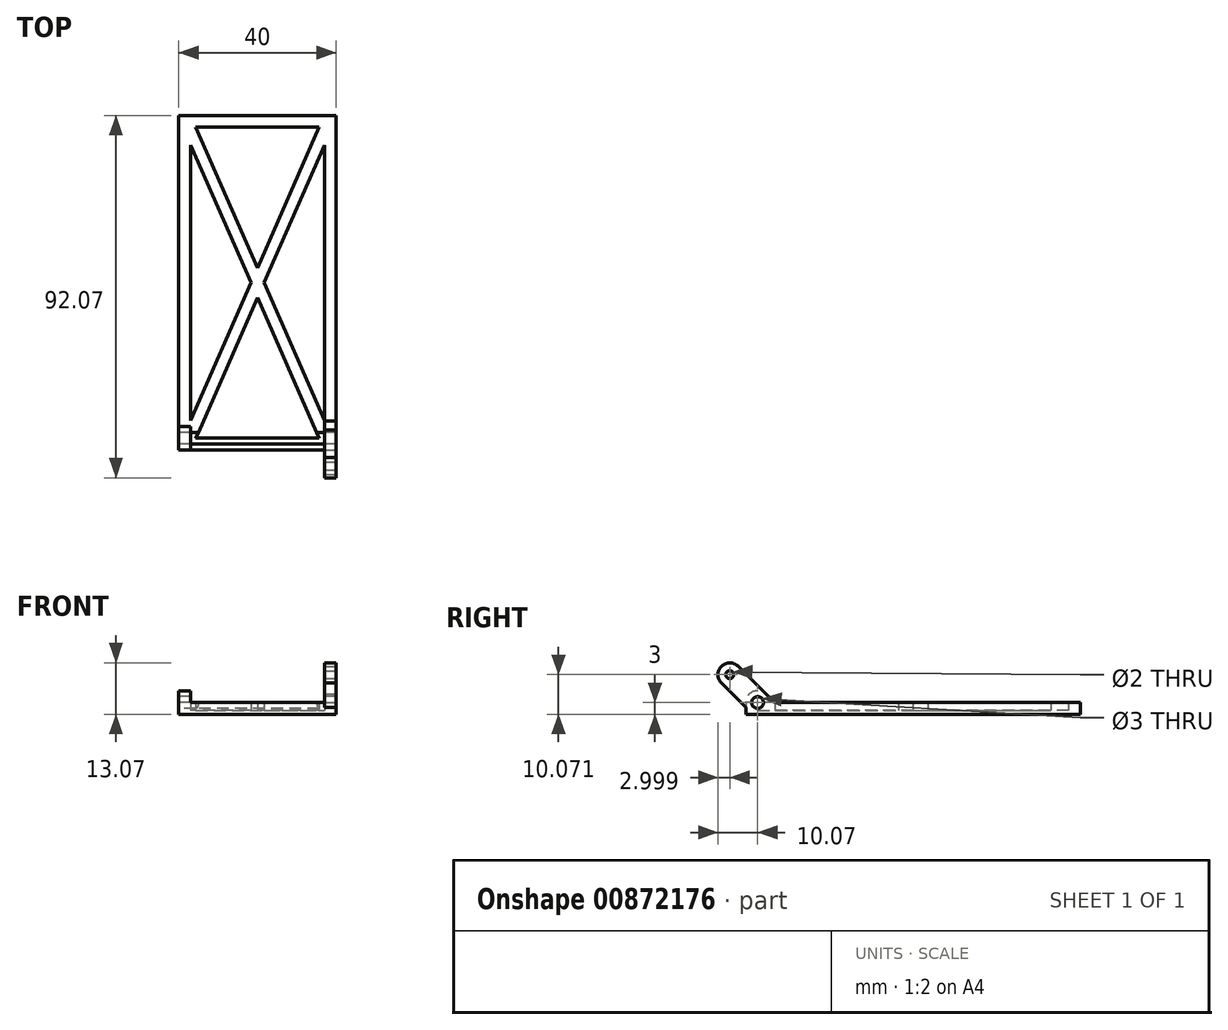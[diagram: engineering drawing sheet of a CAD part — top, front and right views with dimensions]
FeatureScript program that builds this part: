
annotation { "Feature Type Name" : "Feature", "Feature Type Description" : "" }
export const myFeature = defineFeature(function(context is Context, id is Id, definition is map)
    precondition{}
    {
        {
            var Q0;
            Q0=qCreatedBy(makeId("Top.planeOp"),FACE);
            var sketch = newSketch(context, id + "F0", { "sketchPlane" : qUnion([Q0])});
            skLineSegment(sketch, "E0.bottom", {"start": v(20, 42.5) * mm, "end": v(-20, 42.5) * mm});
            skLineSegment(sketch, "E0.top", {"start": v(20, -42.5) * mm, "end": v(-20, -42.5) * mm});
            skLineSegment(sketch, "E0.left", {"start": v(20, 42.5) * mm, "end": v(20, -42.5) * mm});
            skLineSegment(sketch, "E0.right", {"start": v(-20, 42.5) * mm, "end": v(-20, -42.5) * mm});
            skPoint(sketch, "E0.middle", {"position": v(0, 0) * mm});
            skSolve(sketch);
        }
        {
            var Q0;
            Q0=makeQuery(id+"F0.imprint","IMPRINT",FACE,{"disambiguationData":[TD([[makeQuery(id+"F0.imprint","IMPRINT",EDGE,{"derivedFrom":sQuery(id+"F0.wireOp",EDGE,"E0.bottom")}),1.0]])]});
            extrude(context, id + "F1", {"entities" : qUnion([Q0]), "depth" : 1 * mm, "offsetDistance" : 25 * mm});
        }
        {
            var Q0;
            Q0=makeQuery(id+"F1.opExtrude","CAP_FACE",FACE,{"disambiguationData":[OSD([sQuery(id+"F0.wireOp",EDGE,"E0.bottom"),sQuery(id+"F0.wireOp",EDGE,"E0.top"),sQuery(id+"F0.wireOp",EDGE,"E0.left"),sQuery(id+"F0.wireOp",EDGE,"E0.right")])],"isStart":false});
            var sketch = newSketch(context, id + "F2", { "sketchPlane" : qUnion([Q0])});
            skLineSegment(sketch, "E1.bottom", {"start": v(17, -42.5) * mm, "end": v(20, -42.5) * mm});
            skLineSegment(sketch, "E1.top", {"start": v(17, 42.5) * mm, "end": v(20, 42.5) * mm});
            skLineSegment(sketch, "E1.left", {"start": v(17, -42.5) * mm, "end": v(17, 42.5) * mm});
            skLineSegment(sketch, "E1.right", {"start": v(20, -42.5) * mm, "end": v(20, 42.5) * mm});
            skLineSegment(sketch, "E2.bottom", {"start": v(-20, -42.5) * mm, "end": v(-17, -42.5) * mm});
            skLineSegment(sketch, "E2.top", {"start": v(-20, 42.5) * mm, "end": v(-17, 42.5) * mm});
            skLineSegment(sketch, "E2.left", {"start": v(-20, -42.5) * mm, "end": v(-20, 42.5) * mm});
            skLineSegment(sketch, "E2.right", {"start": v(-17, -42.5) * mm, "end": v(-17, 42.5) * mm});
            skLineSegment(sketch, "E3", {"start": v(-17, -42.5) * mm, "end": v(17, 35.03) * mm});
            skLineSegment(sketch, "E4", {"start": v(17, 35.03) * mm, "end": v(17, 42.5) * mm});
            skLineSegment(sketch, "E5", {"start": v(17, 42.5) * mm, "end": v(-17, -35.03) * mm});
            skLineSegment(sketch, "E6", {"start": v(-17, -35.03) * mm, "end": v(-17, -42.5) * mm});
            skLineSegment(sketch, "E7", {"start": v(17, -42.5) * mm, "end": v(-17, 35.03) * mm});
            skLineSegment(sketch, "E8", {"start": v(-17, 35.03) * mm, "end": v(-17, 42.5) * mm});
            skLineSegment(sketch, "E9", {"start": v(-17, 42.5) * mm, "end": v(17, -35.03) * mm});
            skLineSegment(sketch, "E10", {"start": v(17, -35.03) * mm, "end": v(17, -42.5) * mm});
            skLineSegment(sketch, "E11.bottom", {"start": v(-20, -42.5) * mm, "end": v(20, -42.5) * mm});
            skLineSegment(sketch, "E11.top", {"start": v(-20, -39.5) * mm, "end": v(20, -39.5) * mm});
            skLineSegment(sketch, "E11.left", {"start": v(-20, -42.5) * mm, "end": v(-20, -39.5) * mm});
            skLineSegment(sketch, "E11.right", {"start": v(20, -42.5) * mm, "end": v(20, -39.5) * mm});
            skLineSegment(sketch, "E12.bottom", {"start": v(-20, 42.5) * mm, "end": v(20, 42.5) * mm});
            skLineSegment(sketch, "E12.top", {"start": v(-20, 39.5) * mm, "end": v(20, 39.5) * mm});
            skLineSegment(sketch, "E12.left", {"start": v(-20, 42.5) * mm, "end": v(-20, 39.5) * mm});
            skLineSegment(sketch, "E12.right", {"start": v(20, 42.5) * mm, "end": v(20, 39.5) * mm});
            skSolve(sketch);
        }
        {
            var Q0;
            {var subQ0=sQuery(id+"F2.wireOp",EDGE,"E11.bottom");Q0=makeQuery(id+"F2.imprint","IMPRINT",FACE,{"disambiguationData":[TD([[makeQuery(id+"F2.imprint","IMPRINT",EDGE,{"derivedFrom":subQ0}),-1.0]])]});}
            var Q1;
            {var subQ0=sQuery(id+"F2.wireOp",EDGE,"E3");var subQ3=sQuery(id+"F2.wireOp",EDGE,"E11.top");var subQ5=makeQuery(id+"F2.imprint","INTERSECT",VERTEX,{"derivedFrom":[subQ0,subQ3]});Q1=makeQuery(id+"F2.imprint","IMPRINT",FACE,{"disambiguationData":[TD([[makeQuery(id+"F2.imprint","IMPRINT",EDGE,{"disambiguationData":[TD([[subQ5,1.0]])],"derivedFrom":subQ3}),-1.0]])]});}
            var Q2;
            {var subQ0=sQuery(id+"F2.wireOp",EDGE,"E2.bottom");Q2=makeQuery(id+"F2.imprint","IMPRINT",FACE,{"disambiguationData":[TD([[makeQuery(id+"F2.imprint","IMPRINT",EDGE,{"derivedFrom":subQ0}),-1.0]])]});}
            var Q3;
            {var subQ0=sQuery(id+"F2.wireOp",EDGE,"E7");var subQ3=sQuery(id+"F2.wireOp",EDGE,"E11.top");var subQ5=makeQuery(id+"F2.imprint","INTERSECT",VERTEX,{"derivedFrom":[subQ0,subQ3]});Q3=makeQuery(id+"F2.imprint","IMPRINT",FACE,{"disambiguationData":[TD([[makeQuery(id+"F2.imprint","IMPRINT",EDGE,{"disambiguationData":[TD([[subQ5,-1.0]])],"derivedFrom":subQ3}),-1.0]])]});}
            var Q4;
            {var subQ0=sQuery(id+"F2.wireOp",EDGE,"E1.bottom");Q4=makeQuery(id+"F2.imprint","IMPRINT",FACE,{"disambiguationData":[TD([[makeQuery(id+"F2.imprint","IMPRINT",EDGE,{"derivedFrom":subQ0}),-1.0]])]});}
            var Q5;
            {var subQ0=sQuery(id+"F2.wireOp",EDGE,"E1.left");var subQ1=makeQuery(id+"F2.imprint","INTERSECT",VERTEX,{"derivedFrom":[subQ0,sQuery(id+"F2.wireOp",EDGE,"E9")]});Q5=makeQuery(id+"F2.imprint","IMPRINT",FACE,{"disambiguationData":[TD([[makeQuery(id+"F2.imprint","IMPRINT",EDGE,{"disambiguationData":[TD([[subQ1,-1.0]])],"derivedFrom":subQ0}),-1.0]])]});}
            var Q6;
            {var subQ0=sQuery(id+"F2.wireOp",EDGE,"E9");var subQ1=sQuery(id+"F2.wireOp",EDGE,"E1.left");var subQ2=makeQuery(id+"F2.imprint","INTERSECT",VERTEX,{"derivedFrom":[subQ1,subQ0]});Q6=makeQuery(id+"F2.imprint","IMPRINT",FACE,{"disambiguationData":[TD([[makeQuery(id+"F2.imprint","IMPRINT",EDGE,{"disambiguationData":[TD([[subQ2,1.0]])],"derivedFrom":subQ1}),1.0]])]});}
            var Q7;
            {var subQ3=sQuery(id+"F2.wireOp",EDGE,"E5");var subQ7=sQuery(id+"F2.wireOp",EDGE,"E2.right");var subQ9=makeQuery(id+"F2.imprint","INTERSECT",VERTEX,{"derivedFrom":[subQ7,subQ3]});Q7=makeQuery(id+"F2.imprint","IMPRINT",FACE,{"disambiguationData":[TD([[makeQuery(id+"F2.imprint","IMPRINT",EDGE,{"disambiguationData":[TD([[subQ9,1.0]])],"derivedFrom":subQ7}),-1.0]])]});}
            var Q8;
            {var subQ2=sQuery(id+"F2.wireOp",EDGE,"E12.top");var subQ7=sQuery(id+"F2.wireOp",EDGE,"E2.left");var subQ9=makeQuery(id+"F2.imprint","INTERSECT",VERTEX,{"derivedFrom":[subQ7,subQ2]});Q8=makeQuery(id+"F2.imprint","IMPRINT",FACE,{"disambiguationData":[TD([[makeQuery(id+"F2.imprint","IMPRINT",EDGE,{"disambiguationData":[TD([[subQ9,-1.0]])],"derivedFrom":subQ7}),1.0]])]});}
            var Q9;
            {var subQ0=sQuery(id+"F2.wireOp",EDGE,"E7");var subQ1=sQuery(id+"F2.wireOp",EDGE,"E3");var subQ2=makeQuery(id+"F2.imprint","INTERSECT",VERTEX,{"derivedFrom":[subQ1,subQ0]});Q9=makeQuery(id+"F2.imprint","IMPRINT",FACE,{"disambiguationData":[TD([[makeQuery(id+"F2.imprint","IMPRINT",EDGE,{"disambiguationData":[TD([[subQ2,-1.0]])],"derivedFrom":subQ1}),1.0]])]});}
            var Q10;
            {var subQ0=sQuery(id+"F2.wireOp",EDGE,"E7");var subQ1=sQuery(id+"F2.wireOp",EDGE,"E2.right");var subQ2=makeQuery(id+"F2.imprint","INTERSECT",VERTEX,{"derivedFrom":[subQ1,subQ0]});Q10=makeQuery(id+"F2.imprint","IMPRINT",FACE,{"disambiguationData":[TD([[makeQuery(id+"F2.imprint","IMPRINT",EDGE,{"disambiguationData":[TD([[subQ2,-1.0]])],"derivedFrom":subQ1}),-1.0]])]});}
            var Q11;
            {var subQ1=sQuery(id+"F2.wireOp",EDGE,"E3");var subQ7=sQuery(id+"F2.wireOp",EDGE,"E1.left");var subQ9=makeQuery(id+"F2.imprint","INTERSECT",VERTEX,{"derivedFrom":[subQ7,subQ1]});Q11=makeQuery(id+"F2.imprint","IMPRINT",FACE,{"disambiguationData":[TD([[makeQuery(id+"F2.imprint","IMPRINT",EDGE,{"disambiguationData":[TD([[subQ9,-1.0]])],"derivedFrom":subQ7}),1.0]])]});}
            var Q12;
            {var subQ0=sQuery(id+"F2.wireOp",EDGE,"E2.top");Q12=makeQuery(id+"F2.imprint","IMPRINT",FACE,{"disambiguationData":[TD([[makeQuery(id+"F2.imprint","IMPRINT",EDGE,{"derivedFrom":subQ0}),1.0]])]});}
            var Q13;
            {var subQ0=sQuery(id+"F2.wireOp",EDGE,"E9");var subQ3=sQuery(id+"F2.wireOp",EDGE,"E12.top");var subQ5=makeQuery(id+"F2.imprint","INTERSECT",VERTEX,{"derivedFrom":[subQ0,subQ3]});Q13=makeQuery(id+"F2.imprint","IMPRINT",FACE,{"disambiguationData":[TD([[makeQuery(id+"F2.imprint","IMPRINT",EDGE,{"disambiguationData":[TD([[subQ5,1.0]])],"derivedFrom":subQ3}),1.0]])]});}
            var Q14;
            {var subQ0=sQuery(id+"F2.wireOp",EDGE,"E12.bottom");Q14=makeQuery(id+"F2.imprint","IMPRINT",FACE,{"disambiguationData":[TD([[makeQuery(id+"F2.imprint","IMPRINT",EDGE,{"derivedFrom":subQ0}),1.0]])]});}
            var Q15;
            {var subQ0=sQuery(id+"F2.wireOp",EDGE,"E5");var subQ3=sQuery(id+"F2.wireOp",EDGE,"E12.top");var subQ5=makeQuery(id+"F2.imprint","INTERSECT",VERTEX,{"derivedFrom":[subQ0,subQ3]});Q15=makeQuery(id+"F2.imprint","IMPRINT",FACE,{"disambiguationData":[TD([[makeQuery(id+"F2.imprint","IMPRINT",EDGE,{"disambiguationData":[TD([[subQ5,-1.0]])],"derivedFrom":subQ3}),1.0]])]});}
            var Q16;
            {var subQ0=sQuery(id+"F2.wireOp",EDGE,"E1.top");Q16=makeQuery(id+"F2.imprint","IMPRINT",FACE,{"disambiguationData":[TD([[makeQuery(id+"F2.imprint","IMPRINT",EDGE,{"derivedFrom":subQ0}),1.0]])]});}
            extrude(context, id + "F3", {"entities" : qUnion([Q0, Q1, Q2, Q3, Q4, Q5, Q6, Q7, Q8, Q9, Q10, Q11, Q12, Q13, Q14, Q15, Q16]), "operationType" : NewBodyOperationType.ADD, "depth" : 2 * mm, "offsetDistance" : 25 * mm});
        }
        {
            var Q0;
            Q0=makeQuery(id+"F3.boolean.opBoolean","MERGE",FACE,{"derivedFrom":[makeQuery(id+"F1.opExtrude","SWEPT_FACE",FACE,{"disambiguationData":[OSD([sQuery(id+"F0.wireOp",EDGE,"E0.left")])]}),makeQuery(id+"F3.opExtrude","SWEPT_FACE",FACE,{"disambiguationData":[OSD([sQuery(id+"F2.wireOp",EDGE,"E1.right")])]})]});
            var sketch = newSketch(context, id + "F4", { "sketchPlane" : qUnion([Q0])});
            skCircle(sketch, "E13", {"center": v(-39.5, 3) * mm, "radius": 3 * mm});
            skLineSegment(sketch, "E14", {"start": v(-39.5, 3) * mm, "end": v(-46.57, 10.07) * mm});
            skLineSegment(sketch, "E15", {"start": v(-48.65, 7.91) * mm, "end": v(-44.41, 12.15) * mm});
            skLineSegment(sketch, "E16", {"start": v(-44.41, 12.15) * mm, "end": v(-37.42, 5.16) * mm});
            skLineSegment(sketch, "E17", {"start": v(-48.65, 7.91) * mm, "end": v(-41.62, 0.88) * mm});
            skCircle(sketch, "E18", {"center": v(-46.57, 10.07) * mm, "radius": 3 * mm});
            skCircle(sketch, "E19", {"center": v(-46.57, 10.07) * mm, "radius": 1 * mm});
            skLineSegment(sketch, "E20", {"start": v(-37.42, 5.16) * mm, "end": v(-35.18, 3) * mm});
            skSolve(sketch);
        }
        {
            var Q0;
            {var subQ3=sQuery(id+"F4.wireOp",EDGE,"E14");var subQ8=sQuery(id+"F4.wireOp",EDGE,"E13");var subQ9=makeQuery(id+"F4.imprint","INTERSECT",VERTEX,{"derivedFrom":[subQ8,subQ3]});Q0=makeQuery(id+"F4.imprint","IMPRINT",FACE,{"disambiguationData":[TD([[makeQuery(id+"F4.imprint","IMPRINT",EDGE,{"disambiguationData":[TD([[subQ9,-1.0]])],"derivedFrom":subQ3}),1.0]])]});}
            var Q1;
            {var subQ0=sQuery(id+"F4.wireOp",EDGE,"E13");var subQ4=sQuery(id+"F4.wireOp",EDGE,"E14");var subQ6=makeQuery(id+"F4.imprint","INTERSECT",VERTEX,{"derivedFrom":[subQ0,subQ4]});Q1=makeQuery(id+"F4.imprint","IMPRINT",FACE,{"disambiguationData":[TD([[makeQuery(id+"F4.imprint","IMPRINT",EDGE,{"disambiguationData":[TD([[subQ6,1.0]])],"derivedFrom":subQ0}),1.0]])]});}
            var Q2;
            {var subQ0=sQuery(id+"F4.wireOp",EDGE,"E13");var subQ4=sQuery(id+"F4.wireOp",EDGE,"E14");var subQ5=makeQuery(id+"F4.imprint","INTERSECT",VERTEX,{"derivedFrom":[subQ0,subQ4]});Q2=makeQuery(id+"F4.imprint","IMPRINT",FACE,{"disambiguationData":[TD([[makeQuery(id+"F4.imprint","IMPRINT",EDGE,{"disambiguationData":[TD([[subQ5,1.0]])],"derivedFrom":subQ4}),1.0]])]});}
            var Q3;
            {var subQ0=sQuery(id+"F4.wireOp",EDGE,"E20");Q3=makeQuery(id+"F4.imprint","IMPRINT",FACE,{"disambiguationData":[TD([[makeQuery(id+"F4.imprint","IMPRINT",EDGE,{"derivedFrom":subQ0}),-1.0]])]});}
            var Q4;
            {var subQ1=sQuery(id+"F4.wireOp",EDGE,"E13");var subQ3=sQuery(id+"F4.wireOp",EDGE,"E14");var subQ4=makeQuery(id+"F4.imprint","INTERSECT",VERTEX,{"derivedFrom":[subQ1,subQ3]});Q4=makeQuery(id+"F4.imprint","IMPRINT",FACE,{"disambiguationData":[TD([[makeQuery(id+"F4.imprint","IMPRINT",EDGE,{"disambiguationData":[TD([[subQ4,-1.0]])],"derivedFrom":subQ3}),-1.0]])]});}
            var Q5;
            {var subQ0=sQuery(id+"F4.wireOp",EDGE,"E18");var subQ3=sQuery(id+"F4.wireOp",EDGE,"E14");var subQ4=makeQuery(id+"F4.imprint","INTERSECT",VERTEX,{"derivedFrom":[subQ3,subQ0]});Q5=makeQuery(id+"F4.imprint","IMPRINT",FACE,{"disambiguationData":[TD([[makeQuery(id+"F4.imprint","IMPRINT",EDGE,{"disambiguationData":[TD([[subQ4,-1.0]])],"derivedFrom":subQ3}),-1.0]])]});}
            var Q6;
            {var subQ0=sQuery(id+"F4.wireOp",EDGE,"E18");var subQ1=sQuery(id+"F4.wireOp",EDGE,"E14");var subQ2=makeQuery(id+"F4.imprint","INTERSECT",VERTEX,{"derivedFrom":[subQ1,subQ0]});Q6=makeQuery(id+"F4.imprint","IMPRINT",FACE,{"disambiguationData":[TD([[makeQuery(id+"F4.imprint","IMPRINT",EDGE,{"disambiguationData":[TD([[subQ2,-1.0]])],"derivedFrom":subQ1}),1.0]])]});}
            var Q7;
            {var subQ0=sQuery(id+"F4.wireOp",EDGE,"E16");var subQ1=sQuery(id+"F4.wireOp",EDGE,"E15");var subQ2=makeQuery(id+"F4.imprint","INTERSECT",VERTEX,{"derivedFrom":[subQ1,subQ0]});Q7=makeQuery(id+"F4.imprint","IMPRINT",FACE,{"disambiguationData":[TD([[makeQuery(id+"F4.imprint","IMPRINT",EDGE,{"disambiguationData":[TD([[subQ2,1.0]])],"derivedFrom":subQ1}),1.0]])]});}
            extrude(context, id + "F5", {"entities" : qUnion([Q0, Q1, Q2, Q3, Q4, Q5, Q6, Q7]), "oppositeDirection" : true, "depth" : 3 * mm, "offsetDistance" : 25 * mm});
        }
        {
            var Q0;
            Q0=makeQuery(id+"F3.boolean.opBoolean","MERGE",FACE,{"derivedFrom":[makeQuery(id+"F1.opExtrude","SWEPT_FACE",FACE,{"disambiguationData":[OSD([sQuery(id+"F0.wireOp",EDGE,"E0.right")])]}),makeQuery(id+"F3.opExtrude","SWEPT_FACE",FACE,{"disambiguationData":[OSD([sQuery(id+"F2.wireOp",EDGE,"E2.left")])]})]});
            var sketch = newSketch(context, id + "F6", { "sketchPlane" : qUnion([Q0])});
            skCircle(sketch, "E21", {"center": v(39.5, 3) * mm, "radius": 3 * mm});
            skSolve(sketch);
        }
        {
            var Q0;
            {var subQ0=sQuery(id+"F6.wireOp",EDGE,"E21");var subQ1=sQuery(id+"F2.wireOp",EDGE,"E2.left");var subQ2=makeQuery(id+"F3.opExtrude","CAP_EDGE",EDGE,{"disambiguationData":[OSD([subQ1])],"isStart":false});var subQ4=makeQuery(id+"F6.imprint","INTERSECT",VERTEX,{"derivedFrom":[subQ2,subQ0]});Q0=makeQuery(id+"F6.imprint","IMPRINT",FACE,{"disambiguationData":[TD([[makeQuery(id+"F6.imprint","IMPRINT",EDGE,{"disambiguationData":[TD([[subQ4,1.0]])],"derivedFrom":subQ0}),1.0]])]});}
            extrude(context, id + "F7", {"entities" : qUnion([Q0]), "oppositeDirection" : true, "depth" : 3 * mm, "offsetDistance" : 25 * mm});
        }
        {
            var Q0;
            Q0=makeQuery(id+"F1.opExtrude","SWEPT_BODY",BODY,{"disambiguationData":[OSD([sQuery(id+"F0.wireOp",EDGE,"E0.bottom"),sQuery(id+"F0.wireOp",EDGE,"E0.top"),sQuery(id+"F0.wireOp",EDGE,"E0.left"),sQuery(id+"F0.wireOp",EDGE,"E0.right")])]});
            var Q1;
            Q1=makeQuery(id+"F5.opExtrude","SWEPT_BODY",BODY,{"disambiguationData":[OSD([sQuery(id+"F0.wireOp",EDGE,"E0.top"),sQuery(id+"F0.wireOp",EDGE,"E0.left"),sQuery(id+"F2.wireOp",EDGE,"E1.bottom"),sQuery(id+"F2.wireOp",EDGE,"E1.right"),sQuery(id+"F4.wireOp",EDGE,"E16"),sQuery(id+"F4.wireOp",EDGE,"E17"),sQuery(id+"F4.wireOp",EDGE,"E18"),sQuery(id+"F4.wireOp",EDGE,"E19"),sQuery(id+"F4.wireOp",EDGE,"E20")])]});
            var Q2;
            Q2=makeQuery(id+"F7.opExtrude","SWEPT_BODY",BODY,{"disambiguationData":[OSD([sQuery(id+"F2.wireOp",EDGE,"E2.left"),sQuery(id+"F6.wireOp",EDGE,"E21")])]});
            booleanBodies(context, id + "F8", {"operationType" : BooleanOperationType.UNION, "tools" : qUnion([Q0, Q1, Q2])});
        }
        {
            var Q0;
            {var subQ0=sQuery(id+"F2.wireOp",EDGE,"E2.left");Q0=makeQuery(id+"F8.opBoolean","MERGE",FACE,{"derivedFrom":[makeQuery(id+"F3.boolean.opBoolean","MERGE",FACE,{"derivedFrom":[makeQuery(id+"F1.opExtrude","SWEPT_FACE",FACE,{"disambiguationData":[OSD([sQuery(id+"F0.wireOp",EDGE,"E0.right")])]}),makeQuery(id+"F3.opExtrude","SWEPT_FACE",FACE,{"disambiguationData":[OSD([subQ0])]})]}),makeQuery(id+"F7.opExtrude","CAP_FACE",FACE,{"disambiguationData":[OSD([subQ0,sQuery(id+"F6.wireOp",EDGE,"E21")])],"isStart":true})]});}
            var sketch = newSketch(context, id + "F9", { "sketchPlane" : qUnion([Q0])});
            skCircle(sketch, "E22", {"center": v(39.5, 3) * mm, "radius": 1.5 * mm});
            skSolve(sketch);
        }
        {
            var Q0;
            Q0=makeQuery(id+"F9.imprint","IMPRINT",FACE,{"disambiguationData":[TD([[makeQuery(id+"F9.imprint","IMPRINT",EDGE,{"derivedFrom":sQuery(id+"F9.wireOp",EDGE,"E22")}),1.0]])]});
            extrude(context, id + "F10", {"entities" : qUnion([Q0]), "operationType" : NewBodyOperationType.REMOVE, "oppositeDirection" : true, "depth" : 45 * mm, "offsetDistance" : 25 * mm});
        }
    });
